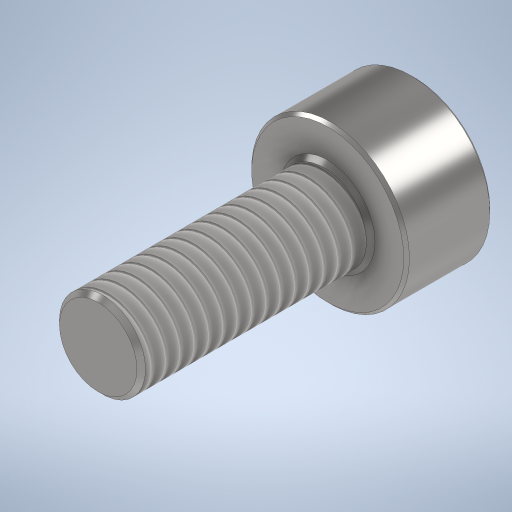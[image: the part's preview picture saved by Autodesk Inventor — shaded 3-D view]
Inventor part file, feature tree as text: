
AUTODESK INVENTOR PART (.ipt)
format: ipt  version: 2024 (Build 280153000, 153)  size: 331,776 bytes
history: native  units: mm
features: extrude x3, chamfer x3, sketch x2, thread x1, hole x1
ambient origin geometry x8: Origin, YZ Plane, XZ Plane, XY Plane, X Axis, Y Axis, Z Axis, Center Point
bodies: Solid1 (feature_tree)
feature tree (10):
  sketch  "Sketch1"  dims[d0=5.5mm d1=3.0mm]
  extrude  "Extrusion1"  Depth=3.0mm
  extrude  "Extrusion2"  Depth=1.5mm TaperAngle=0.0deg
  thread  "Thread1"  [1 undecoded]
  chamfer  "Chamfer1"  Distance=2.5mm
  sketch  "Sketch2"  dims[d2=8.0mm d3=0.0mm d4=3.0mm d5=0.0mm d6=16.0mm d7=0.0mm d8=0.1mm d9=2.0mm d10=45.0deg d11=2.4mm d12=2.5mm d15=0.35mm d16=2.0mm d17=45.0deg d18=3.0mm d19=0.0mm d20=0.15mm d21=2.0mm d22=45.0deg d23=2.4mm d24=6.0mm d25=4.0mm d26=2.0mm d27=90.0deg d28=1.5mm d29=150.0deg]
  hole  "Hole1"  [1 undecoded]
  chamfer  "Chamfer2"  Distance=3.0mm
  extrude  "Extrusion4"  Depth=1.5mm TaperAngle=45.0deg
  chamfer  "Chamfer3"  Distance=2.4mm
note: 2 required parameter values undecoded (feature->parameter linkage not recoverable at this tier; creation-order binding heuristic only, values carry confidence <= 0.55)
